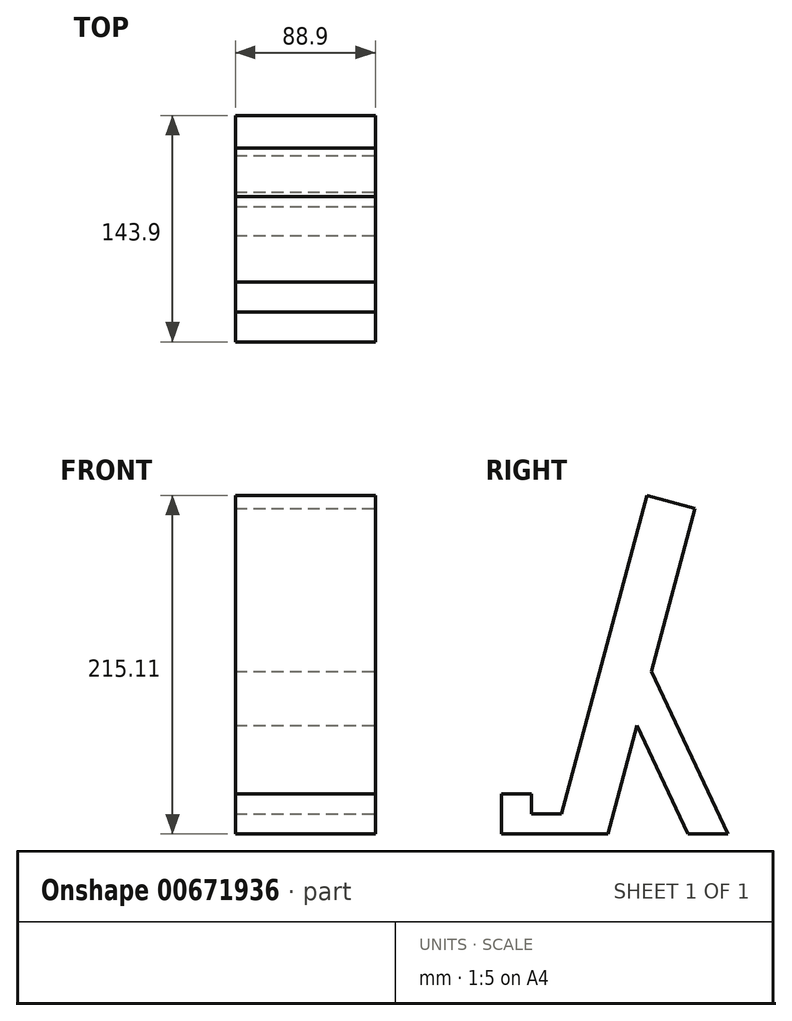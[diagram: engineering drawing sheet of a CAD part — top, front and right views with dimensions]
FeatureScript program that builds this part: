
annotation { "Feature Type Name" : "Feature", "Feature Type Description" : "" }
export const myFeature = defineFeature(function(context is Context, id is Id, definition is map)
    precondition{}
    {
        {
            var Q0;
            Q0=qCreatedBy(makeId("Front.planeOp"),FACE);
            var sketch = newSketch(context, id + "F0", { "sketchPlane" : qUnion([Q0])});
            skLineSegment(sketch, "E0", {"start": v(0, 0) * mm, "end": v(-63.5, 0) * mm});
            skLineSegment(sketch, "E1", {"start": v(-63.5, 0) * mm, "end": v(-63.5, 25.4) * mm});
            skLineSegment(sketch, "E2", {"start": v(0, 0) * mm, "end": v(0, 25.4) * mm});
            skLineSegment(sketch, "E3", {"start": v(0, 25.4) * mm, "end": v(-63.5, 25.4) * mm});
            skSolve(sketch);
        }
        {
            var Q0;
            Q0=makeQuery(id+"F0.imprint","IMPRINT",FACE,{"disambiguationData":[TD([[makeQuery(id+"F0.imprint","IMPRINT",EDGE,{"derivedFrom":sQuery(id+"F0.wireOp",EDGE,"E0")}),-1.0]])]});
            extrude(context, id + "F1", {"entities" : qUnion([Q0]), "depth" : 19.05 * mm, "offsetDistance" : 25.4 * mm});
        }
        {
            var Q0;
            Q0=qCreatedBy(makeId("Right.planeOp"),FACE);
            var sketch = newSketch(context, id + "F2", { "sketchPlane" : qUnion([Q0])});
            skLineSegment(sketch, "E4", {"start": v(0, 0) * mm, "end": v(0, 12.7) * mm});
            skLineSegment(sketch, "E5", {"start": v(0, 12.7) * mm, "end": v(19.05, 12.7) * mm});
            skLineSegment(sketch, "E6", {"start": v(19.05, 12.7) * mm, "end": v(19.05, 0) * mm});
            skLineSegment(sketch, "E7", {"start": v(19.05, 0) * mm, "end": v(0, 0) * mm});
            skLineSegment(sketch, "E8", {"start": v(19.05, 12.7) * mm, "end": v(73.29, 215.1) * mm});
            skLineSegment(sketch, "E9", {"start": v(73.29, 215.1) * mm, "end": v(103.95, 206.9) * mm});
            skLineSegment(sketch, "E10", {"start": v(103.95, 206.9) * mm, "end": v(48.52, 0) * mm});
            skLineSegment(sketch, "E11", {"start": v(48.52, 0) * mm, "end": v(19.05, 0) * mm});
            skSolve(sketch);
        }
        {
            var Q0;
            Q0=makeQuery(id+"F2.imprint","IMPRINT",FACE,{"disambiguationData":[TD([[makeQuery(id+"F2.imprint","IMPRINT",EDGE,{"derivedFrom":sQuery(id+"F2.wireOp",EDGE,"E4")}),-1.0]])]});
            var Q1;
            Q1=makeQuery(id+"F2.imprint","IMPRINT",FACE,{"disambiguationData":[TD([[makeQuery(id+"F2.imprint","IMPRINT",EDGE,{"derivedFrom":sQuery(id+"F2.wireOp",EDGE,"E6")}),1.0]])]});
            extrude(context, id + "F3", {"entities" : qUnion([Q0, Q1]), "operationType" : NewBodyOperationType.ADD, "oppositeDirection" : true, "depth" : 63.5 * mm, "offsetDistance" : 25.4 * mm});
        }
        {
            var Q0;
            Q0=makeQuery(id+"F3.boolean.opBoolean","MERGE",FACE,{"derivedFrom":[makeQuery(id+"F1.opExtrude","SWEPT_FACE",FACE,{"disambiguationData":[OSD([sQuery(id+"F0.wireOp",EDGE,"E2")])]}),makeQuery(id+"F3.opExtrude","CAP_FACE",FACE,{"disambiguationData":[OSD([sQuery(id+"F2.wireOp",EDGE,"E4"),sQuery(id+"F2.wireOp",EDGE,"E5"),sQuery(id+"F2.wireOp",EDGE,"E7"),sQuery(id+"F2.wireOp",EDGE,"E8"),sQuery(id+"F2.wireOp",EDGE,"E9"),sQuery(id+"F2.wireOp",EDGE,"E10"),sQuery(id+"F2.wireOp",EDGE,"E11")])],"isStart":true})]});
            extrude(context, id + "F4", {"entities" : qUnion([Q0]), "operationType" : NewBodyOperationType.ADD, "depth" : 25.4 * mm, "offsetDistance" : 25.4 * mm});
        }
        {
            var Q0;
            Q0=makeQuery(id+"F4.opExtrude","CAP_FACE",FACE,{"disambiguationData":[OSD([sQuery(id+"F0.wireOp",EDGE,"E2"),sQuery(id+"F2.wireOp",EDGE,"E4"),sQuery(id+"F2.wireOp",EDGE,"E5"),sQuery(id+"F2.wireOp",EDGE,"E7"),sQuery(id+"F2.wireOp",EDGE,"E8"),sQuery(id+"F2.wireOp",EDGE,"E9"),sQuery(id+"F2.wireOp",EDGE,"E10"),sQuery(id+"F2.wireOp",EDGE,"E11")])],"isStart":false});
            var sketch = newSketch(context, id + "F5", { "sketchPlane" : qUnion([Q0])});
            skLineSegment(sketch, "E12", {"start": v(76.24, 103.45) * mm, "end": v(124.85, 0) * mm});
            skLineSegment(sketch, "E13", {"start": v(124.85, 0) * mm, "end": v(99.45, 0) * mm});
            skLineSegment(sketch, "E14", {"start": v(99.45, 0) * mm, "end": v(67.01, 69.02) * mm});
            skSolve(sketch);
        }
        {
            var Q0;
            {var subQ0=sQuery(id+"F5.wireOp",EDGE,"E12");Q0=makeQuery(id+"F5.imprint","IMPRINT",FACE,{"disambiguationData":[TD([[makeQuery(id+"F5.imprint","IMPRINT",EDGE,{"derivedFrom":subQ0}),-1.0]])]});}
            extrude(context, id + "F6", {"entities" : qUnion([Q0]), "operationType" : NewBodyOperationType.ADD, "oppositeDirection" : true, "depth" : 88.9 * mm, "offsetDistance" : 25.4 * mm});
        }
    });
